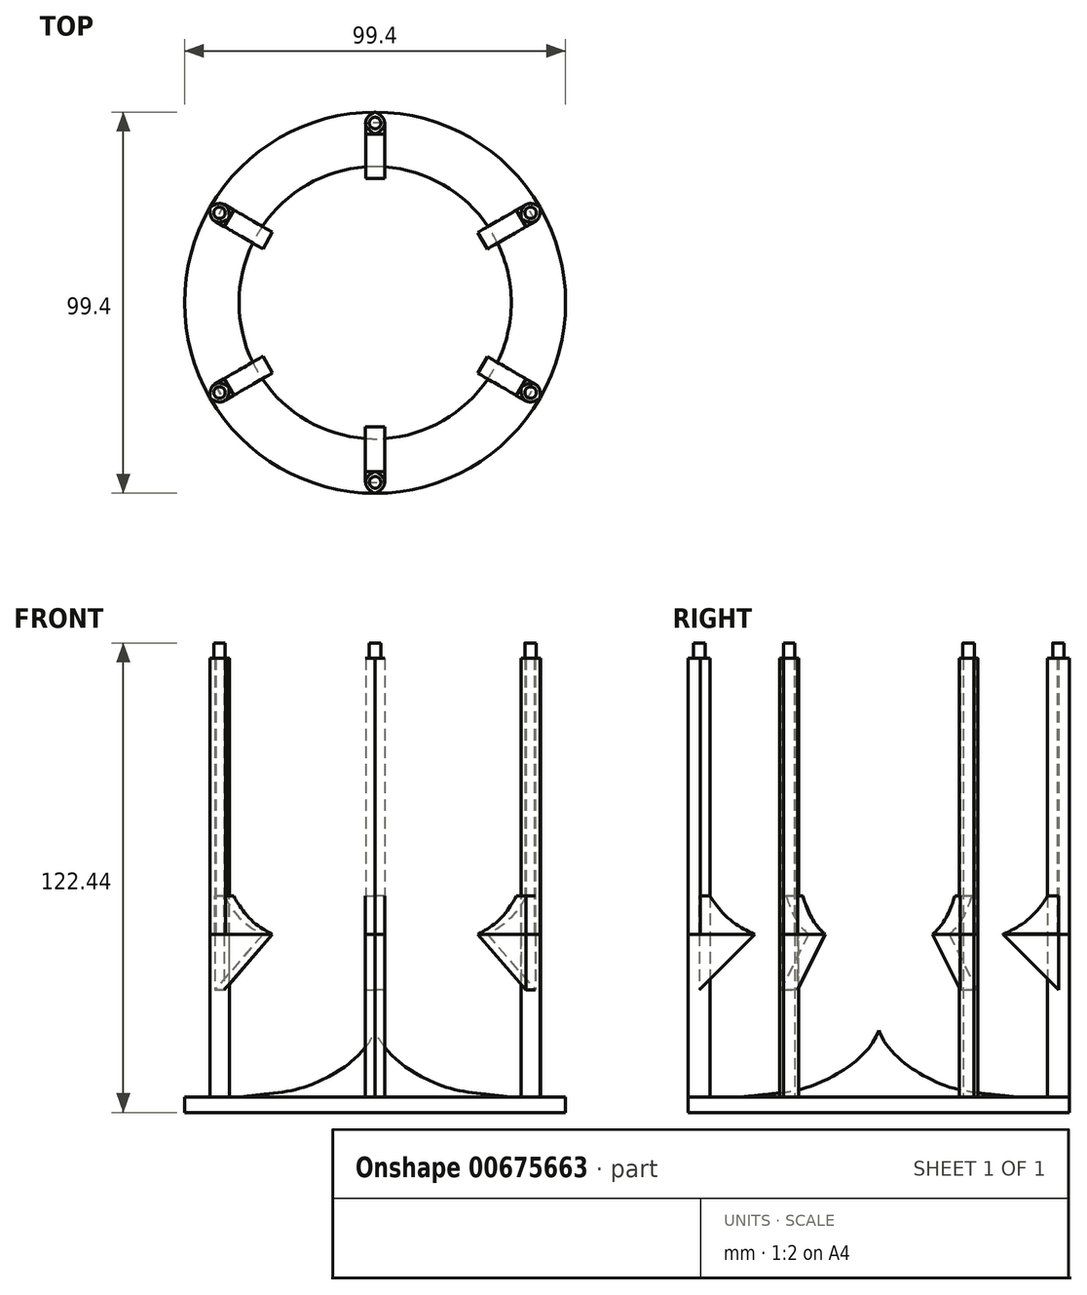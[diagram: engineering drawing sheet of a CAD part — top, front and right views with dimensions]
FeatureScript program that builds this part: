
annotation { "Feature Type Name" : "Feature", "Feature Type Description" : "" }
export const myFeature = defineFeature(function(context is Context, id is Id, definition is map)
    precondition{}
    {
        {
            var Q0;
            Q0=qCreatedBy(makeId("Top.planeOp"),FACE);
            var sketch = newSketch(context, id + "F0", { "sketchPlane" : qUnion([Q0])});
            skCircle(sketch, "E0", {"center": v(0, 0) * mm, "radius": 49.7 * mm});
            skCircle(sketch, "E1", {"center": v(0, 0) * mm, "radius": 44 * mm});
            skSolve(sketch);
        }
        {
            var Q0;
            Q0=makeQuery(id+"F0.imprint","IMPRINT",FACE,{"disambiguationData":[TD([[makeQuery(id+"F0.imprint","IMPRINT",EDGE,{"derivedFrom":sQuery(id+"F0.wireOp",EDGE,"E0")}),1.0]])]});
            var Q1;
            Q1=makeQuery(id+"F0.imprint","IMPRINT",FACE,{"disambiguationData":[TD([[makeQuery(id+"F0.imprint","IMPRINT",EDGE,{"derivedFrom":sQuery(id+"F0.wireOp",EDGE,"E1")}),1.0]])]});
            extrude(context, id + "F1", {"entities" : qUnion([Q0, Q1]), "depth" : 4.03 * mm, "offsetDistance" : 25 * mm});
        }
        {
            var Q0;
            Q0=makeQuery(id+"F1.opExtrude","CAP_FACE",FACE,{"disambiguationData":[OSD([sQuery(id+"F0.wireOp",EDGE,"E0"),sQuery(id+"F0.wireOp",EDGE,"E1")])],"isStart":false});
            var sketch = newSketch(context, id + "F2", { "sketchPlane" : qUnion([Q0])});
            skFitSpline(sketch, "E2", {"points": [v(0, 49.7) * mm, v(2.5, 46.85) * mm, v(0, 44) * mm], "startDerivative": vector(9, -3.6) * mm, "endDerivative": vector(-9, -3.6) * mm});
            skFitSpline(sketch, "E3", {"points": [v(0, 44) * mm, v(-2.5, 46.85) * mm, v(0, 49.7) * mm], "startDerivative": vector(-9, 3.6) * mm, "endDerivative": vector(9, 3.6) * mm});
            skFitSpline(sketch, "E4", {"points": [v(0, -44) * mm, v(2.5, -46.85) * mm, v(0, -49.7) * mm], "startDerivative": vector(9, -3.6) * mm, "endDerivative": vector(-9, -3.6) * mm});
            skFitSpline(sketch, "E5", {"points": [v(0, -49.7) * mm, v(-2.5, -46.85) * mm, v(0, -44) * mm], "startDerivative": vector(-9, 3.6) * mm, "endDerivative": vector(9, 3.6) * mm});
            skFitSpline(sketch, "E6", {"points": [v(38.1, -22) * mm, v(41.82, -21.26) * mm, v(43.04, -24.85) * mm], "startDerivative": vector(7.62, 6) * mm, "endDerivative": vector(-1.38, -9.6) * mm});
            skFitSpline(sketch, "E7", {"points": [v(43.04, -24.85) * mm, v(39.32, -25.59) * mm, v(38.1, -22) * mm], "startDerivative": vector(-7.62, -6) * mm, "endDerivative": vector(1.38, 9.6) * mm});
            skLineSegment(sketch, "E8.0", {"start": v(43.04, -24.85) * mm, "end": v(44.3, -22.68) * mm, "construction": true});
            skLineSegment(sketch, "E8.1", {"start": v(44.3, -22.68) * mm, "end": v(41.82, -21.26) * mm, "construction": true});
            skLineSegment(sketch, "E8.8", {"start": v(41.8, -27.01) * mm, "end": v(43.04, -24.85) * mm, "construction": true});
            skLineSegment(sketch, "E8.9", {"start": v(41.8, -27.01) * mm, "end": v(39.32, -25.59) * mm, "construction": true});
            skLineSegment(sketch, "E8.16", {"start": v(43.04, -24.85) * mm, "end": v(43.8, -23.55) * mm, "construction": true});
            skLineSegment(sketch, "E8.17", {"start": v(43.8, -23.55) * mm, "end": v(43.27, -23.25) * mm, "construction": true});
            skLineSegment(sketch, "E8.24", {"start": v(42.3, -26.15) * mm, "end": v(43.04, -24.85) * mm, "construction": true});
            skLineSegment(sketch, "E8.25", {"start": v(42.3, -26.15) * mm, "end": v(41.77, -25.85) * mm, "construction": true});
            skLineSegment(sketch, "E8.32", {"start": v(43.04, -24.85) * mm, "end": v(43.8, -23.55) * mm, "construction": true});
            skLineSegment(sketch, "E8.33", {"start": v(43.8, -23.55) * mm, "end": v(39.37, -21) * mm, "construction": true});
            skLineSegment(sketch, "E8.40", {"start": v(42.3, -26.15) * mm, "end": v(43.04, -24.85) * mm, "construction": true});
            skLineSegment(sketch, "E8.41", {"start": v(42.3, -26.15) * mm, "end": v(37.87, -23.6) * mm, "construction": true});
            skFitSpline(sketch, "E9", {"points": [v(38.1, 22) * mm, v(39.32, 25.59) * mm, v(43.04, 24.85) * mm], "startDerivative": vector(-1.38, 9.6) * mm, "endDerivative": vector(7.62, -6) * mm});
            skFitSpline(sketch, "E10", {"points": [v(43.04, 24.85) * mm, v(41.82, 21.26) * mm, v(38.1, 22) * mm], "startDerivative": vector(1.38, -9.6) * mm, "endDerivative": vector(-7.62, 6) * mm});
            skLineSegment(sketch, "E11.0", {"start": v(43.04, 24.85) * mm, "end": v(41.8, 27.01) * mm, "construction": true});
            skLineSegment(sketch, "E11.1", {"start": v(41.8, 27.01) * mm, "end": v(39.32, 25.59) * mm, "construction": true});
            skLineSegment(sketch, "E11.8", {"start": v(44.3, 22.68) * mm, "end": v(43.04, 24.85) * mm, "construction": true});
            skLineSegment(sketch, "E11.9", {"start": v(44.3, 22.68) * mm, "end": v(41.82, 21.26) * mm, "construction": true});
            skLineSegment(sketch, "E11.16", {"start": v(43.04, 24.85) * mm, "end": v(42.3, 26.15) * mm, "construction": true});
            skLineSegment(sketch, "E11.17", {"start": v(42.3, 26.15) * mm, "end": v(41.77, 25.85) * mm, "construction": true});
            skLineSegment(sketch, "E11.24", {"start": v(43.8, 23.55) * mm, "end": v(43.04, 24.85) * mm, "construction": true});
            skLineSegment(sketch, "E11.25", {"start": v(43.8, 23.55) * mm, "end": v(43.27, 23.25) * mm, "construction": true});
            skLineSegment(sketch, "E11.32", {"start": v(43.04, 24.85) * mm, "end": v(42.3, 26.15) * mm, "construction": true});
            skLineSegment(sketch, "E11.33", {"start": v(42.3, 26.15) * mm, "end": v(37.87, 23.6) * mm, "construction": true});
            skLineSegment(sketch, "E11.40", {"start": v(43.8, 23.55) * mm, "end": v(43.04, 24.85) * mm, "construction": true});
            skLineSegment(sketch, "E11.41", {"start": v(43.8, 23.55) * mm, "end": v(39.37, 21) * mm, "construction": true});
            skFitSpline(sketch, "E12", {"points": [v(-38.1, -22) * mm, v(-39.32, -25.6) * mm, v(-43.04, -24.85) * mm], "startDerivative": vector(1.38, -9.6) * mm, "endDerivative": vector(-7.62, 6) * mm});
            skFitSpline(sketch, "E13", {"points": [v(-43.04, -24.85) * mm, v(-41.82, -21.26) * mm, v(-38.1, -22) * mm], "startDerivative": vector(-1.38, 9.6) * mm, "endDerivative": vector(7.62, -6) * mm});
            skLineSegment(sketch, "E14.0", {"start": v(-43.04, -24.85) * mm, "end": v(-41.8, -27.02) * mm, "construction": true});
            skLineSegment(sketch, "E14.1", {"start": v(-41.8, -27.02) * mm, "end": v(-39.32, -25.6) * mm, "construction": true});
            skLineSegment(sketch, "E14.8", {"start": v(-44.3, -22.69) * mm, "end": v(-43.04, -24.85) * mm, "construction": true});
            skLineSegment(sketch, "E14.9", {"start": v(-44.3, -22.69) * mm, "end": v(-41.82, -21.26) * mm, "construction": true});
            skLineSegment(sketch, "E14.16", {"start": v(-43.04, -24.85) * mm, "end": v(-42.3, -26.15) * mm, "construction": true});
            skLineSegment(sketch, "E14.17", {"start": v(-42.3, -26.15) * mm, "end": v(-41.77, -25.85) * mm, "construction": true});
            skLineSegment(sketch, "E14.24", {"start": v(-43.8, -23.55) * mm, "end": v(-43.04, -24.85) * mm, "construction": true});
            skLineSegment(sketch, "E14.25", {"start": v(-43.8, -23.55) * mm, "end": v(-43.27, -23.25) * mm, "construction": true});
            skLineSegment(sketch, "E14.32", {"start": v(-43.04, -24.85) * mm, "end": v(-42.3, -26.15) * mm, "construction": true});
            skLineSegment(sketch, "E14.33", {"start": v(-42.3, -26.15) * mm, "end": v(-37.87, -23.6) * mm, "construction": true});
            skLineSegment(sketch, "E14.40", {"start": v(-43.8, -23.55) * mm, "end": v(-43.04, -24.85) * mm, "construction": true});
            skLineSegment(sketch, "E14.41", {"start": v(-43.8, -23.55) * mm, "end": v(-39.37, -21) * mm, "construction": true});
            skFitSpline(sketch, "E15", {"points": [v(-38.1, 22) * mm, v(-41.82, 21.26) * mm, v(-43.04, 24.85) * mm], "startDerivative": vector(-7.62, -6) * mm, "endDerivative": vector(1.38, 9.6) * mm});
            skFitSpline(sketch, "E16", {"points": [v(-43.04, 24.85) * mm, v(-39.32, 25.59) * mm, v(-38.1, 22) * mm], "startDerivative": vector(7.62, 6) * mm, "endDerivative": vector(-1.38, -9.6) * mm});
            skLineSegment(sketch, "E17.0", {"start": v(-43.04, 24.85) * mm, "end": v(-44.3, 22.68) * mm, "construction": true});
            skLineSegment(sketch, "E17.1", {"start": v(-44.3, 22.68) * mm, "end": v(-41.82, 21.26) * mm, "construction": true});
            skLineSegment(sketch, "E17.8", {"start": v(-41.8, 27.01) * mm, "end": v(-43.04, 24.85) * mm, "construction": true});
            skLineSegment(sketch, "E17.9", {"start": v(-41.8, 27.01) * mm, "end": v(-39.32, 25.59) * mm, "construction": true});
            skLineSegment(sketch, "E17.16", {"start": v(-43.04, 24.85) * mm, "end": v(-43.8, 23.55) * mm, "construction": true});
            skLineSegment(sketch, "E17.17", {"start": v(-43.8, 23.55) * mm, "end": v(-43.27, 23.25) * mm, "construction": true});
            skLineSegment(sketch, "E17.24", {"start": v(-42.3, 26.15) * mm, "end": v(-43.04, 24.85) * mm, "construction": true});
            skLineSegment(sketch, "E17.25", {"start": v(-42.3, 26.15) * mm, "end": v(-41.77, 25.85) * mm, "construction": true});
            skLineSegment(sketch, "E17.32", {"start": v(-43.04, 24.85) * mm, "end": v(-43.8, 23.55) * mm, "construction": true});
            skLineSegment(sketch, "E17.33", {"start": v(-43.8, 23.55) * mm, "end": v(-39.37, 21) * mm, "construction": true});
            skLineSegment(sketch, "E17.40", {"start": v(-42.3, 26.15) * mm, "end": v(-43.04, 24.85) * mm, "construction": true});
            skLineSegment(sketch, "E17.41", {"start": v(-42.3, 26.15) * mm, "end": v(-37.87, 23.6) * mm, "construction": true});
            skLineSegment(sketch, "E18", {"start": v(-39.32, 25.59) * mm, "end": v(-41.82, 21.26) * mm});
            skLineSegment(sketch, "E19", {"start": v(-39.32, 25.59) * mm, "end": v(-26.46, 18.16) * mm});
            skLineSegment(sketch, "E20", {"start": v(-41.82, 21.26) * mm, "end": v(-28.96, 13.83) * mm});
            skLineSegment(sketch, "E21", {"start": v(-26.46, 18.16) * mm, "end": v(-28.96, 13.83) * mm});
            skLineSegment(sketch, "E22", {"start": v(-2.5, 46.85) * mm, "end": v(2.5, 46.85) * mm});
            skLineSegment(sketch, "E23", {"start": v(2.5, 46.85) * mm, "end": v(2.5, 32) * mm});
            skLineSegment(sketch, "E24", {"start": v(2.5, 32) * mm, "end": v(-2.5, 32) * mm});
            skLineSegment(sketch, "E25", {"start": v(-2.5, 46.85) * mm, "end": v(-2.5, 32) * mm});
            skLineSegment(sketch, "E26", {"start": v(39.32, 25.59) * mm, "end": v(41.82, 21.26) * mm});
            skLineSegment(sketch, "E27", {"start": v(41.82, 21.26) * mm, "end": v(28.96, 13.83) * mm});
            skLineSegment(sketch, "E28", {"start": v(28.96, 13.83) * mm, "end": v(26.46, 18.16) * mm});
            skLineSegment(sketch, "E29", {"start": v(39.32, 25.59) * mm, "end": v(26.46, 18.16) * mm});
            skLineSegment(sketch, "E30", {"start": v(26.46, -18.17) * mm, "end": v(28.96, -13.84) * mm});
            skLineSegment(sketch, "E31", {"start": v(28.96, -13.84) * mm, "end": v(41.82, -21.26) * mm});
            skLineSegment(sketch, "E32", {"start": v(41.82, -21.26) * mm, "end": v(39.32, -25.6) * mm});
            skLineSegment(sketch, "E33", {"start": v(26.46, -18.17) * mm, "end": v(39.32, -25.6) * mm});
            skLineSegment(sketch, "E34", {"start": v(-2.5, -32) * mm, "end": v(2.5, -32) * mm});
            skLineSegment(sketch, "E35", {"start": v(2.5, -32) * mm, "end": v(2.5, -46.85) * mm});
            skLineSegment(sketch, "E36", {"start": v(2.5, -46.85) * mm, "end": v(-2.5, -46.85) * mm});
            skLineSegment(sketch, "E37", {"start": v(-2.5, -32) * mm, "end": v(-2.5, -46.85) * mm});
            skLineSegment(sketch, "E38", {"start": v(-28.96, -13.83) * mm, "end": v(-26.46, -18.16) * mm});
            skLineSegment(sketch, "E39", {"start": v(-26.46, -18.16) * mm, "end": v(-39.32, -25.59) * mm});
            skLineSegment(sketch, "E40", {"start": v(-39.32, -25.59) * mm, "end": v(-41.82, -21.26) * mm});
            skLineSegment(sketch, "E41", {"start": v(-28.96, -13.83) * mm, "end": v(-41.82, -21.26) * mm});
            skSolve(sketch);
        }
        {
            var Q0;
            Q0=makeQuery(id+"F2.imprint","IMPRINT",FACE,{"disambiguationData":[TD([[makeQuery(id+"F2.imprint","IMPRINT",EDGE,{"derivedFrom":sQuery(id+"F2.wireOp",EDGE,"E15")}),-1.0]])]});
            var Q1;
            Q1=makeQuery(id+"F2.imprint","IMPRINT",FACE,{"disambiguationData":[TD([[makeQuery(id+"F2.imprint","IMPRINT",EDGE,{"derivedFrom":sQuery(id+"F2.wireOp",EDGE,"E2")}),-1.0]])]});
            var Q2;
            Q2=makeQuery(id+"F2.imprint","IMPRINT",FACE,{"disambiguationData":[TD([[makeQuery(id+"F2.imprint","IMPRINT",EDGE,{"derivedFrom":sQuery(id+"F2.wireOp",EDGE,"E9")}),-1.0]])]});
            var Q3;
            Q3=makeQuery(id+"F2.imprint","IMPRINT",FACE,{"disambiguationData":[TD([[makeQuery(id+"F2.imprint","IMPRINT",EDGE,{"derivedFrom":sQuery(id+"F2.wireOp",EDGE,"E6")}),-1.0]])]});
            var Q4;
            Q4=makeQuery(id+"F2.imprint","IMPRINT",FACE,{"disambiguationData":[TD([[makeQuery(id+"F2.imprint","IMPRINT",EDGE,{"derivedFrom":sQuery(id+"F2.wireOp",EDGE,"E4")}),-1.0]])]});
            var Q5;
            Q5=makeQuery(id+"F2.imprint","IMPRINT",FACE,{"disambiguationData":[TD([[makeQuery(id+"F2.imprint","IMPRINT",EDGE,{"derivedFrom":sQuery(id+"F2.wireOp",EDGE,"E12")}),-1.0]])]});
            extrude(context, id + "F3", {"entities" : qUnion([Q0, Q1, Q2, Q3, Q4, Q5]), "operationType" : NewBodyOperationType.ADD, "depth" : 42.4 * mm, "offsetDistance" : 25 * mm});
        }
        {
            var Q0;
            Q0=makeQuery(id+"F3.opExtrude","CAP_FACE",FACE,{"disambiguationData":[OSD([sQuery(id+"F2.wireOp",EDGE,"E15"),sQuery(id+"F2.wireOp",EDGE,"E16")])],"isStart":false});
            var sketch = newSketch(context, id + "F4", { "sketchPlane" : qUnion([Q0])});
            skLineSegment(sketch, "E42", {"start": v(0, 0) * mm, "end": v(0, -44) * mm});
            skLineSegment(sketch, "E43", {"start": v(0, 0) * mm, "end": v(-38.1, -22) * mm});
            skLineSegment(sketch, "E44", {"start": v(-38.1, -22) * mm, "end": v(38.1, 22) * mm});
            skLineSegment(sketch, "E45", {"start": v(0, 0) * mm, "end": v(-38.1, 22) * mm});
            skLineSegment(sketch, "E46", {"start": v(-38.1, 22) * mm, "end": v(38.1, -22) * mm});
            skLineSegment(sketch, "E47", {"start": v(0, 0) * mm, "end": v(0, 44) * mm});
            skFitSpline(sketch, "E48", {"points": [v(0.03, 49.71) * mm, v(2.53, 46.86) * mm, v(0.03, 44.01) * mm], "startDerivative": vector(9, -3.6) * mm, "endDerivative": vector(-9, -3.6) * mm});
            skFitSpline(sketch, "E49", {"points": [v(0.03, 44.01) * mm, v(-2.47, 46.86) * mm, v(0.03, 49.71) * mm], "startDerivative": vector(-9, 3.6) * mm, "endDerivative": vector(9, 3.6) * mm});
            skLineSegment(sketch, "E50", {"start": v(-2.47, 46.86) * mm, "end": v(2.53, 46.86) * mm});
            skLineSegment(sketch, "E51", {"start": v(2.53, 46.86) * mm, "end": v(2.53, 32.36) * mm});
            skLineSegment(sketch, "E52", {"start": v(2.53, 32.36) * mm, "end": v(-2.47, 32.36) * mm});
            skLineSegment(sketch, "E53", {"start": v(-2.47, 46.86) * mm, "end": v(-2.47, 32.36) * mm});
            skSolve(sketch);
        }
        {
            var Q0;
            {var subQ0=sQuery(id+"F4.wireOp",EDGE,"E51");Q0=makeQuery(id+"F4.imprint","IMPRINT",FACE,{"disambiguationData":[TD([[makeQuery(id+"F4.imprint","IMPRINT",EDGE,{"derivedFrom":subQ0}),-1.0]])]});}
            extrude(context, id + "F5", {"entities" : qUnion([Q0]), "operationType" : NewBodyOperationType.ADD, "depth" : 0.1 * mm, "offsetDistance" : 25 * mm});
        }
        {
            var Q0;
            Q0=makeQuery(id+"F5.opExtrude","SWEPT_FACE",FACE,{"disambiguationData":[OSD([sQuery(id+"F4.wireOp",EDGE,"E53")])]});
            var sketch = newSketch(context, id + "F6", { "sketchPlane" : qUnion([Q0])});
            skLineSegment(sketch, "E54", {"start": v(-32.36, 46.44) * mm, "end": v(-46.86, 46.44) * mm});
            skLineSegment(sketch, "E55", {"start": v(-46.86, 46.44) * mm, "end": v(-46.86, 31.94) * mm});
            skLineSegment(sketch, "E56", {"start": v(-32.36, 46.44) * mm, "end": v(-46.86, 31.94) * mm});
            skSolve(sketch);
        }
        {
            var Q0;
            Q0=makeQuery(id+"F6.imprint","IMPRINT",FACE,{"disambiguationData":[TD([[makeQuery(id+"F6.imprint","IMPRINT",EDGE,{"derivedFrom":sQuery(id+"F6.wireOp",EDGE,"E54")}),-1.0]])]});
            extrude(context, id + "F7", {"entities" : qUnion([Q0]), "depth" : -5 * mm, "offsetDistance" : 25 * mm});
        }
        {
            var Q0;
            Q0=makeQuery(id+"F3.opExtrude","CAP_FACE",FACE,{"disambiguationData":[OSD([sQuery(id+"F2.wireOp",EDGE,"E2"),sQuery(id+"F2.wireOp",EDGE,"E3")])],"isStart":false});
            var sketch = newSketch(context, id + "F8", { "sketchPlane" : qUnion([Q0])});
            skFitSpline(sketch, "E57", {"points": [v(0, 49.7) * mm, v(2.5, 46.85) * mm, v(0, 44) * mm], "startDerivative": vector(9, -3.6) * mm, "endDerivative": vector(-9, -3.6) * mm});
            skFitSpline(sketch, "E58", {"points": [v(0, 44) * mm, v(-2.5, 46.85) * mm, v(0, 49.7) * mm], "startDerivative": vector(-9, 3.6) * mm, "endDerivative": vector(9, 3.6) * mm});
            skSolve(sketch);
        }
        {
            var Q0;
            Q0=makeQuery(id+"F8.imprint","IMPRINT",FACE,{"disambiguationData":[TD([[makeQuery(id+"F8.imprint","IMPRINT",EDGE,{"derivedFrom":sQuery(id+"F8.wireOp",EDGE,"E57")}),-1.0]])]});
            extrude(context, id + "F9", {"entities" : qUnion([Q0]), "depth" : 72 * mm, "offsetDistance" : 25 * mm});
        }
        {
            var Q0;
            Q0=makeQuery(id+"F7.opExtrude","CAP_FACE",FACE,{"disambiguationData":[OSD([sQuery(id+"F6.wireOp",EDGE,"E54"),sQuery(id+"F6.wireOp",EDGE,"E55"),sQuery(id+"F6.wireOp",EDGE,"E56")])],"isStart":true});
            var sketch = newSketch(context, id + "F10", { "sketchPlane" : qUnion([Q0])});
            skLineSegment(sketch, "E59", {"start": v(-46.86, 46.44) * mm, "end": v(-46.86, 56.44) * mm});
            skLineSegment(sketch, "E60", {"start": v(-44.01, 46.44) * mm, "end": v(-44.01, 56.44) * mm});
            skFitSpline(sketch, "E61", {"points": [v(-44.01, 56.44) * mm, v(-39.19, 50.54) * mm, v(-32.36, 46.44) * mm], "startDerivative": vector(2.55, -4.3) * mm, "endDerivative": vector(5.39, -2.59) * mm});
            skLineSegment(sketch, "E62", {"start": v(-46.86, 56.44) * mm, "end": v(-44.01, 56.44) * mm});
            skSolve(sketch);
        }
        {
            var Q0;
            {var subQ0=sQuery(id+"F10.wireOp",EDGE,"E60");Q0=makeQuery(id+"F10.imprint","IMPRINT",FACE,{"disambiguationData":[TD([[makeQuery(id+"F10.imprint","IMPRINT",EDGE,{"derivedFrom":subQ0}),-1.0]])]});}
            var Q1;
            {var subQ0=sQuery(id+"F10.wireOp",EDGE,"E59");Q1=makeQuery(id+"F10.imprint","IMPRINT",FACE,{"disambiguationData":[TD([[makeQuery(id+"F10.imprint","IMPRINT",EDGE,{"derivedFrom":subQ0}),-1.0]])]});}
            extrude(context, id + "F11", {"entities" : qUnion([Q0, Q1]), "depth" : -5 * mm, "offsetDistance" : 25 * mm});
        }
        {
            var Q0;
            Q0=makeQuery(id+"F7.opExtrude","SWEPT_BODY",BODY,{"disambiguationData":[OSD([sQuery(id+"F6.wireOp",EDGE,"E54"),sQuery(id+"F6.wireOp",EDGE,"E55"),sQuery(id+"F6.wireOp",EDGE,"E56")])]});
            var Q1;
            Q1=makeQuery(id+"F9.opExtrude","SWEPT_BODY",BODY,{"disambiguationData":[OSD([sQuery(id+"F8.wireOp",EDGE,"E57"),sQuery(id+"F8.wireOp",EDGE,"E58")])]});
            var Q2;
            Q2=makeQuery(id+"F11.opExtrude","SWEPT_BODY",BODY,{"disambiguationData":[OSD([sQuery(id+"F6.wireOp",EDGE,"E54"),sQuery(id+"F10.wireOp",EDGE,"E59"),sQuery(id+"F10.wireOp",EDGE,"E61"),sQuery(id+"F10.wireOp",EDGE,"E62")])]});
            var Q3;
            Q3=makeQuery(id+"F1.opExtrude","SWEPT_FACE",FACE,{"disambiguationData":[OSD([sQuery(id+"F0.wireOp",EDGE,"E0")])]});
            circularPattern(context, id + "F12", {"entities" : qUnion([Q0, Q1, Q2]), "axis" : qUnion([Q3]), "angle" : 360 * degree, "instanceCount" : 6, "equalSpace" : true});
        }
        {
            var Q0;
            Q0=makeQuery(id+"F9.opExtrude","CAP_FACE",FACE,{"disambiguationData":[OSD([sQuery(id+"F8.wireOp",EDGE,"E57"),sQuery(id+"F8.wireOp",EDGE,"E58")])],"isStart":false});
            var sketch = newSketch(context, id + "F13", { "sketchPlane" : qUnion([Q0])});
            skCircle(sketch, "E63", {"center": v(0, 46.85) * mm, "radius": 1.5 * mm});
            skLineSegment(sketch, "E64", {"start": v(0, 44) * mm, "end": v(0, 0) * mm});
            skSolve(sketch);
        }
        {
            var Q0;
            Q0=makeQuery(id+"F13.imprint","IMPRINT",FACE,{"disambiguationData":[TD([[makeQuery(id+"F13.imprint","IMPRINT",EDGE,{"derivedFrom":sQuery(id+"F13.wireOp",EDGE,"E63")}),1.0]])]});
            extrude(context, id + "F14", {"entities" : qUnion([Q0]), "operationType" : NewBodyOperationType.ADD, "depth" : 4 * mm, "offsetDistance" : 25 * mm});
        }
        {
            var Q0;
            Q0=makeQuery(id+"F9.opExtrude","SWEPT_BODY",BODY,{"disambiguationData":[OSD([sQuery(id+"F8.wireOp",EDGE,"E57"),sQuery(id+"F8.wireOp",EDGE,"E58")])]});
            var Q1;
            Q1=makeQuery(id+"F1.opExtrude","SWEPT_FACE",FACE,{"disambiguationData":[OSD([sQuery(id+"F0.wireOp",EDGE,"E0")])]});
            circularPattern(context, id + "F15", {"entities" : qUnion([Q0]), "axis" : qUnion([Q1]), "angle" : 360 * degree, "instanceCount" : 6, "equalSpace" : true});
        }
        {
            var Q0;
            Q0=makeQuery(id+"F7.opExtrude","SWEPT_BODY",BODY,{"disambiguationData":[OSD([sQuery(id+"F6.wireOp",EDGE,"E54"),sQuery(id+"F6.wireOp",EDGE,"E55"),sQuery(id+"F6.wireOp",EDGE,"E56")])]});
            var Q1;
            Q1=makeQuery(id+"F11.opExtrude","SWEPT_BODY",BODY,{"disambiguationData":[OSD([sQuery(id+"F6.wireOp",EDGE,"E54"),sQuery(id+"F10.wireOp",EDGE,"E59"),sQuery(id+"F10.wireOp",EDGE,"E61"),sQuery(id+"F10.wireOp",EDGE,"E62")])]});
            var Q2;
            Q2=makeQuery(id+"F9.opExtrude","SWEPT_BODY",BODY,{"disambiguationData":[OSD([sQuery(id+"F8.wireOp",EDGE,"E57"),sQuery(id+"F8.wireOp",EDGE,"E58")])]});
            var Q3;
            Q3=makeQuery(id+"F1.opExtrude","SWEPT_FACE",FACE,{"disambiguationData":[OSD([sQuery(id+"F0.wireOp",EDGE,"E0")])]});
            circularPattern(context, id + "F16", {"entities" : qUnion([Q0, Q1, Q2]), "axis" : qUnion([Q3]), "angle" : 360 * degree, "instanceCount" : 6, "equalSpace" : true});
        }
        {
            var Q0;
            Q0=qCreatedBy(makeId("Right.planeOp"),FACE);
            var sketch = newSketch(context, id + "F17", { "sketchPlane" : qUnion([Q0])});
            skLineSegment(sketch, "E65", {"start": v(0, 0) * mm, "end": v(44, 4.03) * mm});
            skLineSegment(sketch, "E66", {"start": v(0, 0) * mm, "end": v(-44, 4.03) * mm});
            skLineSegment(sketch, "E67", {"start": v(0, 0) * mm, "end": v(0, 21.45) * mm});
            skLineSegment(sketch, "E68", {"start": v(0, 0) * mm, "end": v(35.5, 4.03) * mm});
            skLineSegment(sketch, "E69", {"start": v(35.5, 4.03) * mm, "end": v(0, 4.03) * mm});
            skFitSpline(sketch, "E70", {"points": [v(35.5, 4.03) * mm, v(26.22, 5.03) * mm, v(18.5, 6.58) * mm, v(12.03, 9.43) * mm, v(6.85, 12.73) * mm, v(2.4, 17.13) * mm, v(0, 21.45) * mm], "startDerivative": vector(-68.57, 8.12) * mm, "endDerivative": vector(-13.37, 35.14) * mm});
            skSolve(sketch);
        }
        {
            var Q0;
            {var subQ2=sQuery(id+"F17.wireOp",EDGE,"E69");Q0=makeQuery(id+"F17.imprint","IMPRINT",FACE,{"disambiguationData":[TD([[makeQuery(id+"F17.imprint","IMPRINT",EDGE,{"derivedFrom":subQ2}),-1.0]])]});}
            var Q1;
            Q1=makeQuery(id+"F1.opExtrude","SWEPT_FACE",FACE,{"disambiguationData":[OSD([sQuery(id+"F0.wireOp",EDGE,"E0")])]});
            revolve(context, id + "F18", {"operationType" : NewBodyOperationType.ADD, "entities" : qUnion([Q0]), "axis" : qUnion([Q1]), "revolveType" : RevolveType.FULL});
        }
    });
